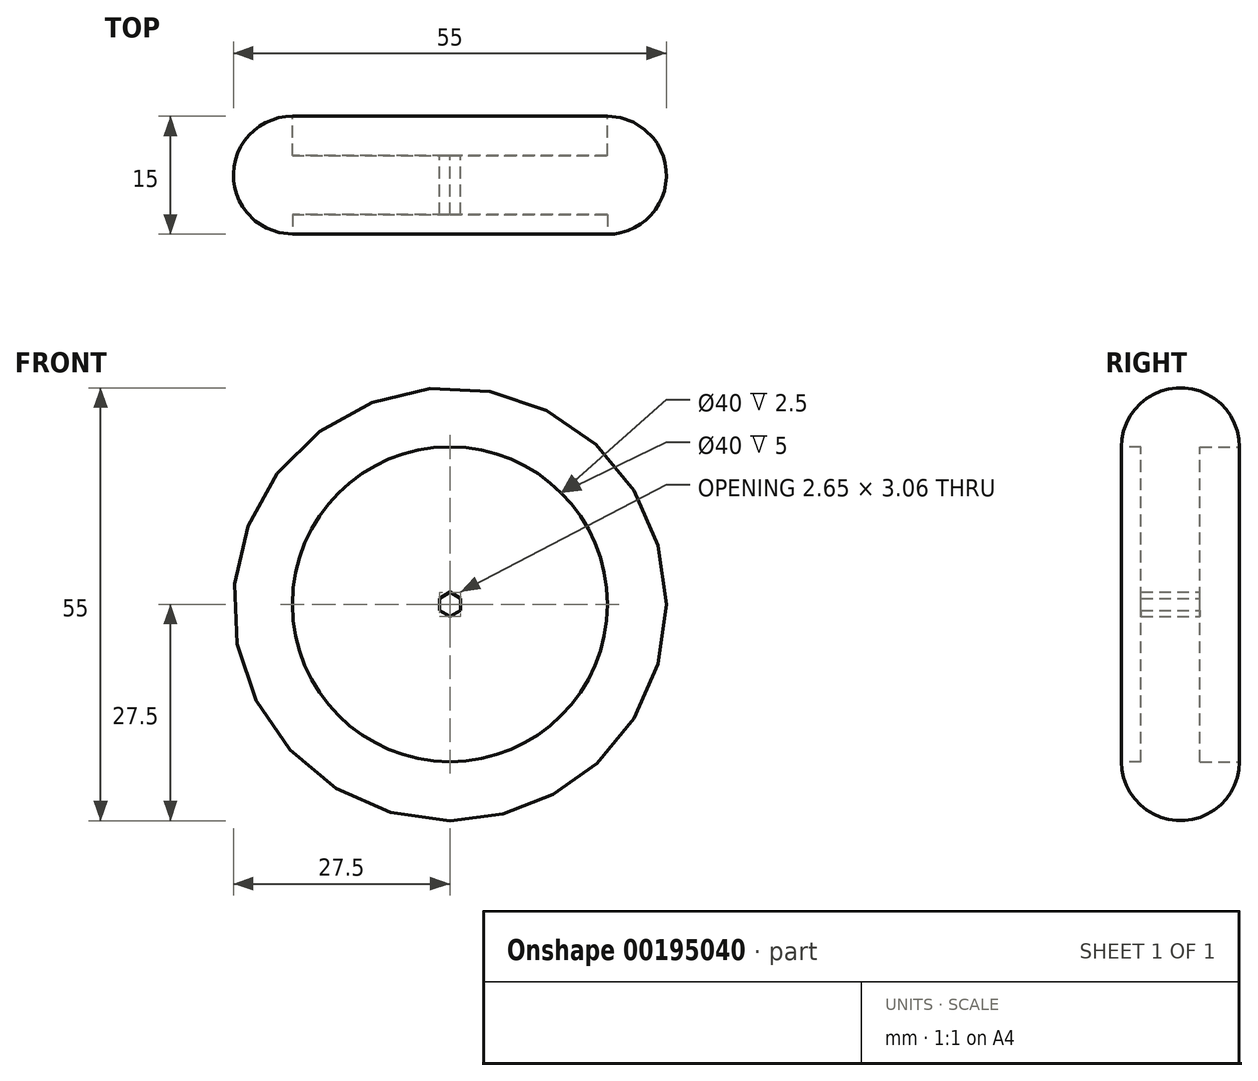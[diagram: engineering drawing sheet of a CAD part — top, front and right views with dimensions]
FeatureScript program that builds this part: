
annotation { "Feature Type Name" : "Feature", "Feature Type Description" : "" }
export const myFeature = defineFeature(function(context is Context, id is Id, definition is map)
    precondition{}
    {
        {
            var Q0;
            Q0=qCreatedBy(makeId("Front.planeOp"),FACE);
            var sketch = newSketch(context, id + "F0", { "sketchPlane" : qUnion([Q0])});
            skCircle(sketch, "E0", {"center": v(0, 0) * mm, "radius": 27.5 * mm});
            skCircle(sketch, "E1", {"center": v(0, 0) * mm, "radius": 1.32 * mm});
            skCircle(sketch, "E2.cCircle", {"center": v(0, 0) * mm, "radius": 1.32 * mm, "construction": true});
            skLineSegment(sketch, "E2.0", {"start": v(1.32, 0.76) * mm, "end": v(1.32, -0.76) * mm});
            skLineSegment(sketch, "E2.1", {"start": v(1.32, -0.76) * mm, "end": v(0, -1.53) * mm});
            skLineSegment(sketch, "E2.2", {"start": v(0, -1.53) * mm, "end": v(-1.32, -0.76) * mm});
            skLineSegment(sketch, "E2.3", {"start": v(-1.32, -0.76) * mm, "end": v(-1.33, 0.76) * mm});
            skLineSegment(sketch, "E2.4", {"start": v(-1.33, 0.76) * mm, "end": v(0, 1.53) * mm});
            skLineSegment(sketch, "E2.5", {"start": v(0, 1.53) * mm, "end": v(1.32, 0.76) * mm});
            skPoint(sketch, "E2.0.midPoint", {"position": v(1.32, 0) * mm});
            skSolve(sketch);
        }
        {
            var Q0;
            Q0=makeQuery(id+"F0.imprint","IMPRINT",FACE,{"disambiguationData":[TD([[makeQuery(id+"F0.imprint","IMPRINT",EDGE,{"derivedFrom":sQuery(id+"F0.wireOp",EDGE,"E0")}),1.0]])]});
            extrude(context, id + "F1", {"entities" : qUnion([Q0]), "endBound" : BoundingType.SYMMETRIC, "depth" : 15 * mm});
        }
        {
            var Q0;
            Q0=makeQuery(id+"F1.opExtrude","CAP_EDGE",EDGE,{"disambiguationData":[OSD([sQuery(id+"F0.wireOp",EDGE,"E0")])],"isStart":false});
            var Q1;
            Q1=makeQuery(id+"F1.opExtrude","CAP_EDGE",EDGE,{"disambiguationData":[OSD([sQuery(id+"F0.wireOp",EDGE,"E0")])],"isStart":true});
            fillet(context, id + "F2", {"entities" : qUnion([Q0, Q1]), "radius" : 7.5 * mm, "tangentPropagation" : true, "allowEdgeOverflow" : false});
        }
        {
            var Q0;
            Q0=makeQuery(id+"F1.opExtrude","CAP_FACE",FACE,{"disambiguationData":[OSD([sQuery(id+"F0.wireOp",EDGE,"E0"),sQuery(id+"F0.wireOp",EDGE,"E2.0"),sQuery(id+"F0.wireOp",EDGE,"E2.1"),sQuery(id+"F0.wireOp",EDGE,"E2.2"),sQuery(id+"F0.wireOp",EDGE,"E2.3"),sQuery(id+"F0.wireOp",EDGE,"E2.4"),sQuery(id+"F0.wireOp",EDGE,"E2.5")])],"isStart":false});
            extrude(context, id + "F3", {"entities" : qUnion([Q0]), "operationType" : NewBodyOperationType.REMOVE, "endBound" : BoundingType.SYMMETRIC, "oppositeDirection" : true, "depth" : 5 * mm});
        }
        {
            var Q0;
            Q0=makeQuery(id+"F1.opExtrude","CAP_FACE",FACE,{"disambiguationData":[OSD([sQuery(id+"F0.wireOp",EDGE,"E0"),sQuery(id+"F0.wireOp",EDGE,"E2.0"),sQuery(id+"F0.wireOp",EDGE,"E2.1"),sQuery(id+"F0.wireOp",EDGE,"E2.2"),sQuery(id+"F0.wireOp",EDGE,"E2.3"),sQuery(id+"F0.wireOp",EDGE,"E2.4"),sQuery(id+"F0.wireOp",EDGE,"E2.5")])],"isStart":true});
            extrude(context, id + "F4", {"entities" : qUnion([Q0]), "operationType" : NewBodyOperationType.REMOVE, "oppositeDirection" : true, "depth" : 5 * mm});
        }
    });
